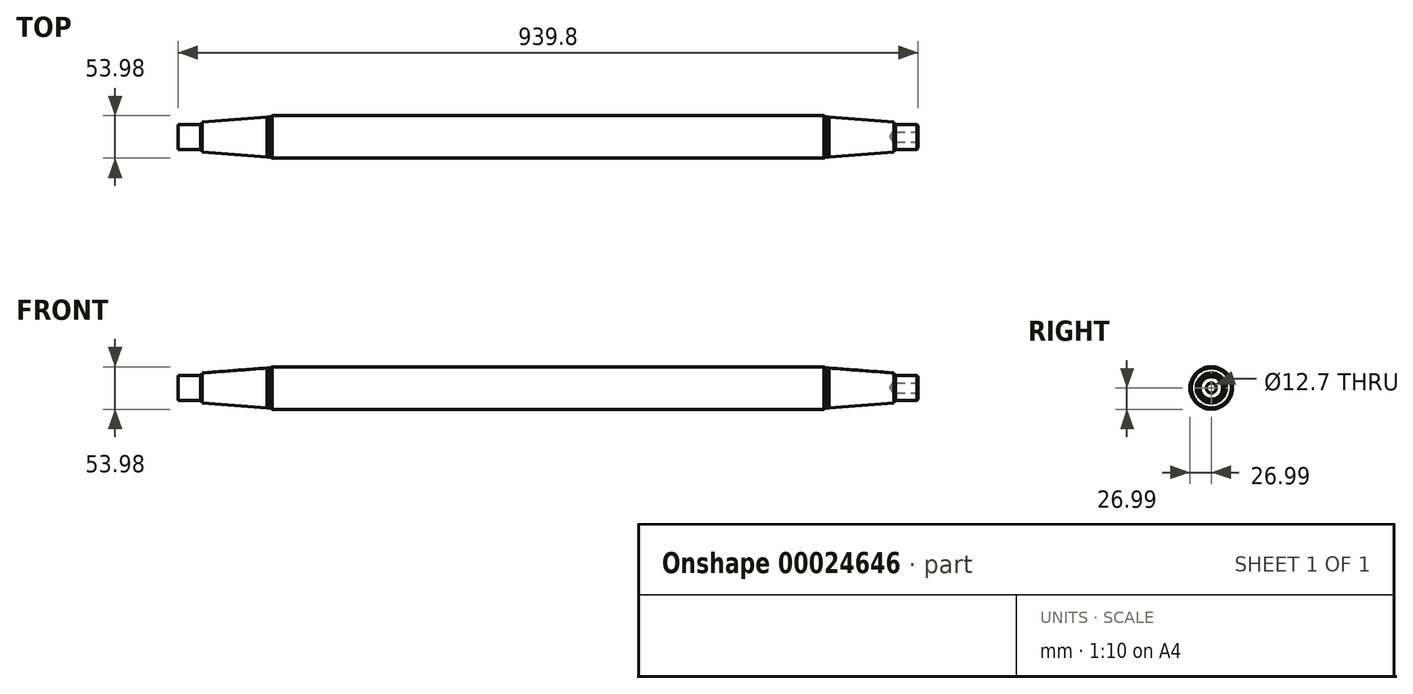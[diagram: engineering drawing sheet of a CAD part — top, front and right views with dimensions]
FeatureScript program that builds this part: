
annotation { "Feature Type Name" : "Feature", "Feature Type Description" : "" }
export const myFeature = defineFeature(function(context is Context, id is Id, definition is map)
    precondition{}
    {
        {
            var Q0;
            Q0=qCreatedBy(makeId("Front.planeOp"),FACE);
            var sketch = newSketch(context, id + "F0", { "sketchPlane" : qUnion([Q0])});
            skLineSegment(sketch, "E0", {"start": v(-469.9, 0) * mm, "end": v(469.9, 0) * mm});
            skLineSegment(sketch, "E1", {"start": v(0, 76.2) * mm, "end": v(0, -76.2) * mm, "construction": true});
            skLineSegment(sketch, "E2", {"start": v(-469.9, 0) * mm, "end": v(-469.9, 15.88) * mm});
            skLineSegment(sketch, "E3.0", {"start": v(-441.32, 14.1) * mm, "end": v(-441.32, 15.88) * mm});
            skLineSegment(sketch, "E4.0", {"start": v(-439.55, 14.1) * mm, "end": v(-439.55, 19.05) * mm});
            skLineSegment(sketch, "E5", {"start": v(-469.9, 15.88) * mm, "end": v(-441.32, 15.88) * mm});
            skLineSegment(sketch, "E6", {"start": v(-441.32, 14.1) * mm, "end": v(-439.55, 14.1) * mm});
            skLineSegment(sketch, "E7", {"start": v(-439.55, 19.05) * mm, "end": v(-357, 25.4) * mm});
            skPoint(sketch, "E8.orphan", {"position": v(-439.55, 0) * mm});
            skLineSegment(sketch, "E9.0", {"start": v(-350.65, 25.4) * mm, "end": v(-350.65, 26.99) * mm});
            skLineSegment(sketch, "E10", {"start": v(-357, 25.4) * mm, "end": v(-353.24, 25.4) * mm});
            skArc(sketch, "E11", {"start": v(-353.82, 25.4) * mm, "mid": v(-352.01, 25.75) * mm, "end": v(-350.65, 26.99) * mm});
            skPoint(sketch, "E12.orphan", {"position": v(-350.65, 25.4) * mm});
            skLineSegment(sketch, "E13", {"start": v(-350.65, 26.99) * mm, "end": v(0, 26.99) * mm});
            skLineSegment(sketch, "E14.MirrorCS", {"start": v(357, 25.4) * mm, "end": v(353.24, 25.4) * mm});
            skLineSegment(sketch, "E15.MirrorCS", {"start": v(350.65, 25.4) * mm, "end": v(350.65, 26.99) * mm});
            skArc(sketch, "E16.MirrorCS", {"start": v(353.82, 25.4) * mm, "mid": v(352.01, 25.75) * mm, "end": v(350.65, 26.99) * mm});
            skLineSegment(sketch, "E17.MirrorCS", {"start": v(441.32, 14.1) * mm, "end": v(441.32, 15.88) * mm});
            skLineSegment(sketch, "E18.MirrorCS", {"start": v(439.55, 14.1) * mm, "end": v(439.55, 19.05) * mm});
            skLineSegment(sketch, "E19.MirrorCS", {"start": v(441.32, 14.1) * mm, "end": v(439.55, 14.1) * mm});
            skLineSegment(sketch, "E20.MirrorCS", {"start": v(469.9, 0) * mm, "end": v(469.9, 15.88) * mm});
            skLineSegment(sketch, "E21.MirrorCS", {"start": v(469.9, 15.88) * mm, "end": v(441.32, 15.88) * mm});
            skLineSegment(sketch, "E22.MirrorCS", {"start": v(439.55, 19.05) * mm, "end": v(357, 25.4) * mm});
            skPoint(sketch, "E23.MirrorP", {"position": v(350.65, 25.4) * mm});
            skPoint(sketch, "E24.MirrorP", {"position": v(439.55, 0) * mm});
            skLineSegment(sketch, "E25.MirrorCS", {"start": v(350.65, 26.99) * mm, "end": v(0, 26.99) * mm});
            skSolve(sketch);
        }
        {
            var Q0;
            Q0=makeQuery(id+"F0.imprint","IMPRINT",FACE,{"disambiguationData":[TD([[makeQuery(id+"F0.imprint","IMPRINT",EDGE,{"derivedFrom":sQuery(id+"F0.wireOp",EDGE,"E0")}),1.0]])]});
            var Q1;
            Q1=sQuery(id+"F0.wireOp",EDGE,"E0");
            revolve(context, id + "F1", {"entities" : qUnion([Q0]), "axis" : qUnion([Q1]), "revolveType" : RevolveType.FULL});
        }
        {
            var Q0;
            Q0=makeQuery(id+"F1.opRevolve","SWEPT_FACE",FACE,{"disambiguationData":[OSD([sQuery(id+"F0.wireOp",EDGE,"E20.MirrorCS")])]});
            var sketch = newSketch(context, id + "F2", { "sketchPlane" : qUnion([Q0])});
            skPoint(sketch, "E26", {"position": v(0, 0) * mm});
            skSolve(sketch);
        }
        {
            var Q0;
            Q0=sQuery(id+"F2.wireOp",VERTEX,"E26");
            var Q1;
            Q1=makeQuery(id+"F1.opRevolve","SWEPT_BODY",BODY,{"disambiguationData":[OSD([sQuery(id+"F0.wireOp",EDGE,"E0"),sQuery(id+"F0.wireOp",EDGE,"E2"),sQuery(id+"F0.wireOp",EDGE,"E3.0"),sQuery(id+"F0.wireOp",EDGE,"E4.0"),sQuery(id+"F0.wireOp",EDGE,"E5"),sQuery(id+"F0.wireOp",EDGE,"E6"),sQuery(id+"F0.wireOp",EDGE,"E7"),sQuery(id+"F0.wireOp",EDGE,"E10"),sQuery(id+"F0.wireOp",EDGE,"E11"),sQuery(id+"F0.wireOp",EDGE,"E13"),sQuery(id+"F0.wireOp",EDGE,"E14.MirrorCS"),sQuery(id+"F0.wireOp",EDGE,"E16.MirrorCS"),sQuery(id+"F0.wireOp",EDGE,"E17.MirrorCS"),sQuery(id+"F0.wireOp",EDGE,"E18.MirrorCS"),sQuery(id+"F0.wireOp",EDGE,"E19.MirrorCS"),sQuery(id+"F0.wireOp",EDGE,"E20.MirrorCS"),sQuery(id+"F0.wireOp",EDGE,"E21.MirrorCS"),sQuery(id+"F0.wireOp",EDGE,"E22.MirrorCS"),sQuery(id+"F0.wireOp",EDGE,"E25.MirrorCS")])]});
            hole(context, id + "F3", {"style" : HoleStyle.SIMPLE, "holeDiameter" : 12.7 * mm, "endStyle" : HoleEndStyle.BLIND, "holeDepth" : 31.75 * mm, "locations" : qUnion([Q0]), "scope" : qUnion([Q1])});
        }
        {
            var Q0;
            Q0=makeQuery(id+"F1.opRevolve","SWEPT_EDGE",EDGE,{"disambiguationData":[OSD([sQuery(id+"F0.wireOp",EDGE,"E20.MirrorCS"),sQuery(id+"F0.wireOp",EDGE,"E21.MirrorCS")])]});
            chamfer(context, id + "F4", {"entities" : qUnion([Q0]), "width" : 1.52 * mm, "tangentPropagation" : true});
        }
    });
